# Revit family: O4UM_NRG
name_source: partatom
category: Mechanical Equipment
units: mm (PartAtom-declared; Revit-internal decimal feet)

## family parameters
Always vertical = Yes
Cut with Voids When Loaded = No
OmniClass Number = 23.40.40.11.17
OmniClass Title = Refrigerated Cases
Part Type = Normal
Room Calculation Point = No
Round Connector Dimension = Use Radius
Shared = No
Work Plane-Based = Yes

## types (12) — shared parameters
12" Shelf = Yes
14" Shelf = Yes
16" Shelf = Yes
18" Shelves = Yes
27" Shelf = Yes
BOTTOM ELECTRICAL = Yes
BOTTOM REFRIGERATION PIPING = Yes
Certifications = NSF 7, UL471, CSA
DATE = 03/31/2016
DESIGNERS NAME = SHIDDRAMESH
DRAIN PIPING = Yes
Default Elevation = 48"
Description = Multi-Deck Merchandiser with Synerg-E™
EQUIPMENT DESCRIPTION = Multi-Deck Merchandiser with Synerg-E™
EQUIPMENT MARK = O4UM-NRG
Electrical plan view = No
GLASS = Glass
Height = 53 5/8"
How Many Defrosts Per Day = 6
Island Discharge Air Velocity (FPM) = 150 FPM
Island Superheat @ Bulb Set Point (°F) = 6-8 °F
Island Timed-Off Fail-Safe (Min) = 40 (Min)
Island Timed-Off Termination Temp (°F) = 42 °F
Item Description = Multi-Deck Merchandiser with Synerg-E™
Legend Number = O4UM-NRG
Manufacturer = HILL PHOENIX
Model = O4UM-NRG
Number of Shelf = 3
PAINTED METAL UPPER SHELF = PAINTED SHELVES
REAR REFRIGERATION PIPING = Yes
REFRIGERATION PIPING = COPPER PIPE
STAINLESS STEEL = GALVANIZED STEEL
Standard Power Amps = 0 A
TOP ELECTRICAL = Yes
TOP REFRIGERATION PIPING = Yes
URL = http://www.hillphoenix.com
Width = 43 1/4"
both shelves visible = Yes
left end = No
left end instance = No

## per-type parameters (varying)
| type | All ends off | DRAIN LINE | High Power (Cornice) Amps | High Power (Cornice) Watts | Island  Case Length | Island Application | Island BTUH Conventional | Island BTUH Parallel | Island Discharge Air(°F) | Island Evaporator (°F) | Island Fans Per Case | Island Front Sill Height | Island High Efficiency Fans Amps | Island High Efficiency Fans Watts | LF STD END | Length | Light Length | Lights Per Row | RT STD END | Refgn | Shelf distance | Standard Power Watts | make not visible on sheet |
| 04' | No | 36" | 0 A | 22 W | 48" | Dairy / Deli / Produce | 1063 | 930 | 31 °F | 28 °F | 1 | All | 0 A | 14 W | Yes | 48" | 48" | 1 | Yes | 22 3/4" | 36" | 11 W | Yes |
| 06' | No | 36" | 0 A | 30 W | 72" | Dairy / Deli / Produce | 1063 | 930 | 31 °F | 28 °F | 2 | All | 0 A | 28 W | Yes | 72" | 36" | 2 | Yes | 28 5/8" | 36" | 17 W | Yes |
| 08' | No | 48" | 0 A | 43 W | 96" | Dairy / Deli / Produce | 1063 | 930 | 31 °F | 28 °F | 2 | All | 0 A | 28 W | Yes | 96" | 48" | 2 | Yes | 28 5/8" | 48" | 24 W | Yes |
| 12' | No | 72" | 1 A | 65 W | 144" | Dairy / Deli / Produce | 1063 | 930 | 31 °F | 28 °F | 3 | All | 1 A | 42 W | Yes | 144" | 48" | 3 | Yes | 28 5/8" | 48" | 36 W | Yes |
| 04' Deli | Yes | 24" | 0 A | 22 W | 48" | Dairy / Deli / Produce | 1063 | 930 | 31 °F | 28 °F | 1 | All | 0 A | 14 W | Yes | 48" | 48" | 1 | Yes | 12 3/8" | 36" | 11 W | No |
| 04' Meat | No | 36" | 0 A | 22 W | 48" | Meat | 1051 | 920 | 30 °F | 26 °F | 1 | Extended | 0 A | 14 W | Yes | 48" | 48" | 1 | Yes | 22 3/4" | 36" | 11 W | Yes |
| 06' Deli | Yes | 36" | 0 A | 30 W | 72" | Dairy / Deli / Produce | 1063 | 930 | 31 °F | 28 °F | 2 | All | 0 A | 28 W | Yes | 72" | 36" | 2 | Yes | 12 3/8" | 36" | 17 W | Yes |
| 06' Meat | No | 36" | 0 A | 30 W | 72" | Meat | 1051 | 920 | 30 °F | 26 °F | 2 | Extended | 0 A | 28 W | Yes | 72" | 36" | 2 | Yes | 28 5/8" | 36" | 17 W | Yes |
| 08' Deli | Yes | 48" | 0 A | 43 W | 96" | Dairy / Deli / Produce | 1063 | 930 | 31 °F | 28 °F | 2 | All | 0 A | 28 W | No | 96" | 48" | 2 | No | 12 3/8" | 48" | 24 W | Yes |
| 08' Meat | No | 48" | 0 A | 43 W | 96" | Meat | 1051 | 920 | 30 °F | 26 °F | 2 | Extended | 0 A | 28 W | Yes | 96" | 48" | 2 | Yes | 28 5/8" | 48" | 24 W | Yes |
| 12' Deli | Yes | 72" | 1 A | 65 W | 144" | Dairy / Deli / Produce | 1063 | 930 | 31 °F | 28 °F | 3 | All | 1 A | 42 W | Yes | 144" | 48" | 3 | Yes | 12 3/8" | 48" | 36 W | Yes |
| 12' Meat | No | 72" | 1 A | 65 W | 144" | Meat | 1051 | 920 | 30 °F | 26 °F | 3 | Extended | 1 A | 42 W | Yes | 144" | 48" | 3 | Yes | 28 5/8" | 48" | 36 W | Yes |

## geometry (parser evidence)
native form markers: Blend x11, Sweep x10
no freeform markers — native parametric forms only
